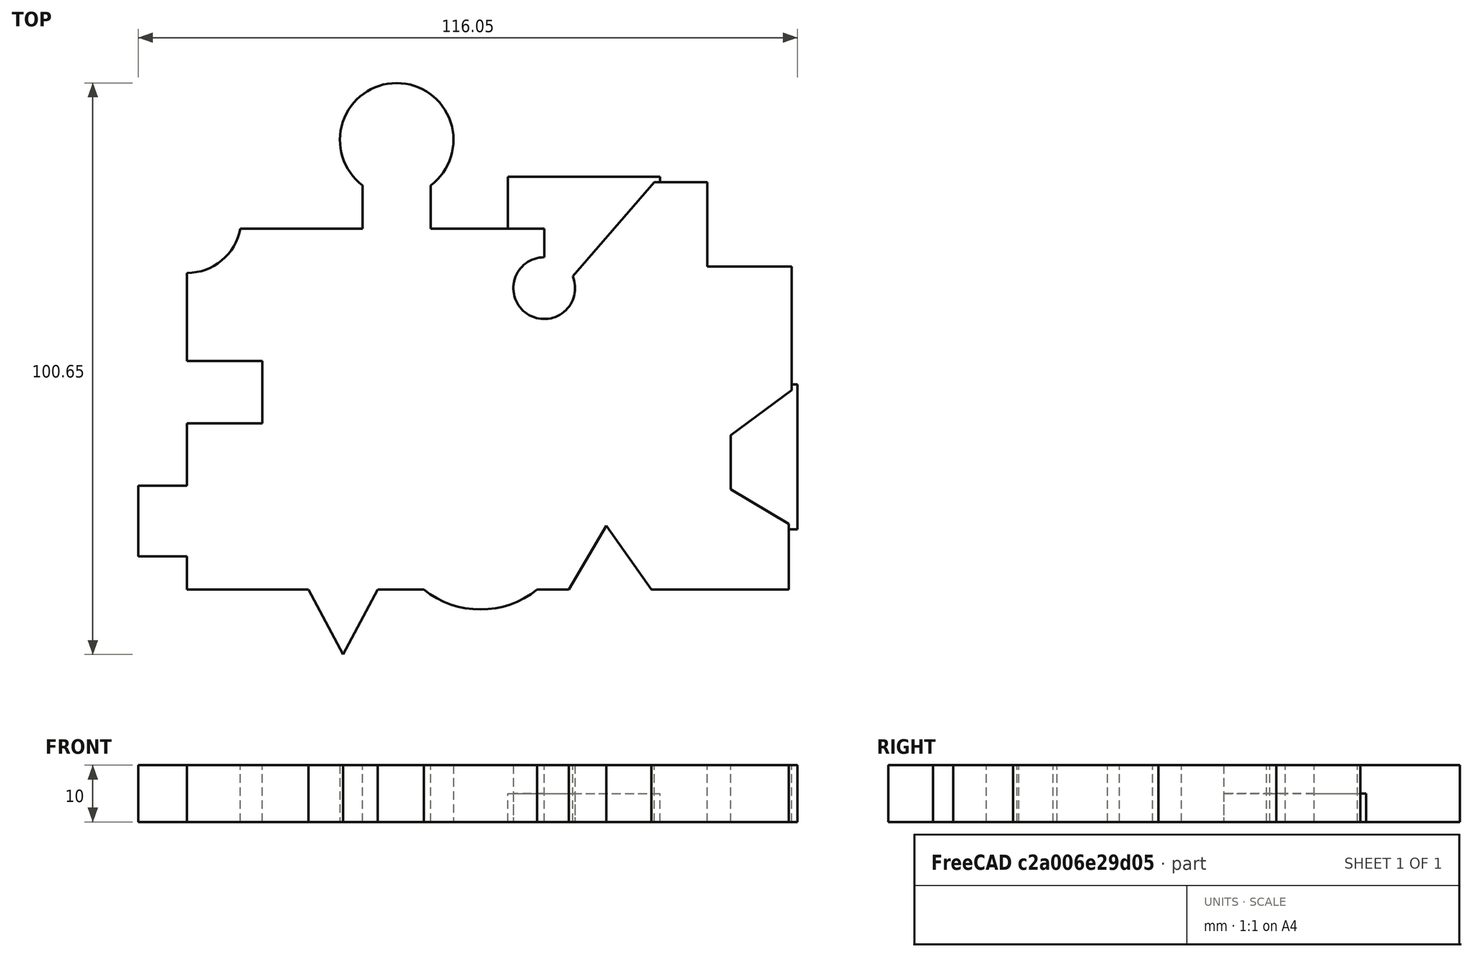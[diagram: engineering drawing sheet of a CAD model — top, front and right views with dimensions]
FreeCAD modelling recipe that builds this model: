
FCSTD DOCUMENT  (FreeCAD 0.19R16345 (Git))
Label: EdgeFeature_0
License: CreativeCommons Attribution
LicenseURL: http://creativecommons.org/licenses/by/4.0/
objects: Part::Feature×2, Sketcher::SketchObject×1, PartDesign::Pad×1, PartDesign::Body×1
note: 6 computed .brp shape members not serialized (recipe doc carries the construction recipe); baked Part::Feature solids carry a one-line shape summary decoded from their .brp

FEATURE [Sketcher::SketchObject] Sketch
  MapMode = 5
  Support = -> [XY_Plane]
  sketch-geometry (35):
    g0: LineSegment StartX=-51.6702 StartY=0 StartZ=0 EndX=-51.6702 EndY=5.85611 EndZ=0
    g1: LineSegment StartX=-51.6702 StartY=29.2851 StartZ=0 EndX=-38.3996 EndY=29.2851 EndZ=0
    g2: LineSegment StartX=-38.3996 StartY=29.2851 StartZ=0 EndX=-38.3996 EndY=40.2372 EndZ=0
    g3: LineSegment StartX=-38.3996 StartY=40.2372 StartZ=0 EndX=-51.6702 EndY=40.2372 EndZ=0
    g4: LineSegment StartX=-51.6702 StartY=40.2372 StartZ=0 EndX=-51.6702 EndY=55.7701 EndZ=0
    g5: ArcOfCircle CenterX=-51.6702 CenterY=65.2959 CenterZ=0 NormalX=0 NormalY=0 NormalZ=1 AngleXU=0 Radius=9.52575 StartAngle=4.71239 EndAngle=6.1035
    g6: LineSegment StartX=11.2262 StartY=63.5934 StartZ=0 EndX=11.2262 EndY=58.5324 EndZ=0
    g7: ArcOfCircle CenterX=11.2262 CenterY=53.0963 CenterZ=0 NormalX=0 NormalY=0 NormalZ=1 AngleXU=0 Radius=5.43607 StartAngle=1.5708 EndAngle=6.68192
    g8: LineSegment StartX=16.2359 StartY=55.2069 StartZ=0 EndX=30.5922 EndY=71.7337 EndZ=0
    g9: LineSegment StartX=30.5922 StartY=71.7337 StartZ=0 EndX=39.9722 EndY=71.7337 EndZ=0
    g10: LineSegment StartX=39.9722 StartY=71.7337 StartZ=0 EndX=39.9722 EndY=56.9026 EndZ=0
    g11: LineSegment StartX=39.9722 StartY=56.9026 StartZ=0 EndX=54.8033 EndY=56.9026 EndZ=0
    g12: LineSegment StartX=54.8033 StartY=56.9026 StartZ=0 EndX=54.8033 EndY=35.144 EndZ=0
    g13: LineSegment StartX=54.8033 StartY=35.144 StartZ=0 EndX=44.0985 EndY=27.1858 EndZ=0
    g14: LineSegment StartX=44.0985 StartY=27.1858 StartZ=0 EndX=44.0985 EndY=17.636 EndZ=0
    g15: LineSegment StartX=44.0985 StartY=17.636 StartZ=0 EndX=54.285 EndY=11.5878 EndZ=0
    g16: LineSegment StartX=54.285 StartY=11.5878 StartZ=0 EndX=54.285 EndY=0 EndZ=0
    g17: LineSegment StartX=54.285 StartY=0 StartZ=0 EndX=30.0921 EndY=0 EndZ=0
    g18: LineSegment StartX=30.0921 StartY=0 StartZ=0 EndX=22.134 EndY=11.2695 EndZ=0
    g19: LineSegment StartX=22.134 StartY=11.2695 StartZ=0 EndX=15.5437 EndY=0 EndZ=0
    g20: LineSegment StartX=-51.6702 StartY=0 StartZ=0 EndX=-30.2666 EndY=0 EndZ=0
    g21: LineSegment StartX=-42.2978 StartY=63.5934 StartZ=0 EndX=-20.755 EndY=63.5934 EndZ=0
    g22: LineSegment StartX=-8.75501 StartY=63.5934 StartZ=0 EndX=11.2262 EndY=63.5934 EndZ=0
    g23: LineSegment StartX=-20.755 StartY=63.5934 StartZ=0 EndX=-20.755 EndY=71.2179 EndZ=0
    g24: ArcOfCircle CenterX=-14.755 CenterY=79.2179 CenterZ=0 NormalX=0 NormalY=0 NormalZ=1 AngleXU=0 Radius=10 StartAngle=5.35589 EndAngle=10.3521
    g25: LineSegment StartX=-8.75501 StartY=71.2179 StartZ=0 EndX=-8.75501 EndY=63.5934 EndZ=0
    g26: LineSegment StartX=-30.2666 StartY=0 StartZ=0 EndX=-24.2206 EndY=-11.4348 EndZ=0
    g27: LineSegment StartX=-24.2206 StartY=-11.4348 StartZ=0 EndX=-18.0945 EndY=0 EndZ=0
    g28: LineSegment StartX=-18.0945 StartY=0 StartZ=0 EndX=-10 EndY=0 EndZ=0
    g29: LineSegment StartX=-51.6702 StartY=18.3059 StartZ=0 EndX=-60.2493 EndY=18.3059 EndZ=0
    g30: LineSegment StartX=-60.2493 StartY=18.3059 StartZ=0 EndX=-60.2493 EndY=5.85611 EndZ=0
    g31: LineSegment StartX=-60.2493 StartY=5.85611 StartZ=0 EndX=-51.6702 EndY=5.85611 EndZ=0
    g32: LineSegment StartX=-51.6702 StartY=18.3059 StartZ=0 EndX=-51.6702 EndY=29.2851 EndZ=0
    g33: ArcOfCircle CenterX=0 CenterY=12.4793 CenterZ=0 NormalX=0 NormalY=0 NormalZ=1 AngleXU=0 Radius=15.9917 StartAngle=4.03684 EndAngle=5.38794
    g34: LineSegment StartX=10 StartY=0 StartZ=0 EndX=15.5437 EndY=0 EndZ=0
  constraints (69):
    c: PointOnObject(g0,g-1)
    c: Vertical(g0)
    c: Coincident(g32,g1)
    c: Coincident(g1,g2)
    c: Coincident(g2,g3)
    c: Horizontal(g3)
    c: Coincident(g3,g4)
    c: Perpendicular(g4,g5) = 4.71239
    c: Perpendicular(g6,g7) = 4.71239
    c: Coincident(g7,g8)
    c: Coincident(g8,g9)
    c: Horizontal(g9)
    c: Coincident(g9,g10)
    c: Vertical(g10)
    c: Coincident(g10,g11)
    c: Horizontal(g11)
    c: Coincident(g11,g12)
    c: Vertical(g12)
    c: Coincident(g12,g13)
    c: Coincident(g13,g14)
    c: Coincident(g14,g15)
    c: Coincident(g15,g16)
    c: PointOnObject(g16,g-1)
    c: Vertical(g16)
    c: Coincident(g16,g17)
    c: PointOnObject(g17,g-1)
    c: Coincident(g17,g18)
    c: Coincident(g18,g19)
    c: PointOnObject(g19,g-1)
    c: Horizontal(g1)
    c: Vertical(g2)
    c: Vertical(g4)
    c: Vertical(g14)
    c: Equal(g3,g1)
    c: Coincident(g20,g0)
    c: Coincident(g34,g19)
    c: Equal(g10,g11)
    c: Vertical(g6)
    c: Coincident(g5,g21)
    c: Coincident(g22,g6)
    c: Horizontal(g22)
    c: Horizontal(g21)
    c: Tangent(g21,g22) = -1.5708
    c: Coincident(g21,g23)
    c: Vertical(g23)
    c: DistanceX(g21,g22) = 12
    c: Coincident(g23,g24)
    c: Coincident(g24,g25)
    c: Vertical(g25)
    c: Coincident(g22,g25)
    c: Radius(g24) = 10
    c: Equal(g23,g25)
    c: Coincident(g26,g27)
    c: Coincident(g20,g26)
    c: Coincident(g28,g27)
    c: Tangent(g20,g28)
    c: Horizontal(g29)
    c: Coincident(g29,g30)
    c: Vertical(g30)
    c: Coincident(g30,g31)
    c: Horizontal(g31)
    c: Coincident(g0,g31)
    c: Coincident(g32,g29)
    c: Tangent(g0,g32)
    c: PointOnObject(g33,g-2)
    c: Coincident(g28,g33)
    c: Coincident(g34,g33)
    c: Tangent(g28,g34)
    c: DistanceX(g33) = 10
FEATURE [PartDesign::Pad] Pad
  Length = 10
  Length2 = 100
  Profile = -> Sketch
  Type = 0
FEATURE [PartDesign::Body] Body  label="EdgeFeature_0"
  Group = -> [Sketch,Pad]
  Origin = -> Origin
  Tip = -> Pad
FEATURE [Part::Feature] Shape
  shape: bbox 26.97 x 25.27 x 5.2 mm, 10 faces (baked)
FEATURE [Part::Feature] Shape001
  shape: bbox 11.9 x 25.76 x 10.2 mm, 10 faces (baked)
